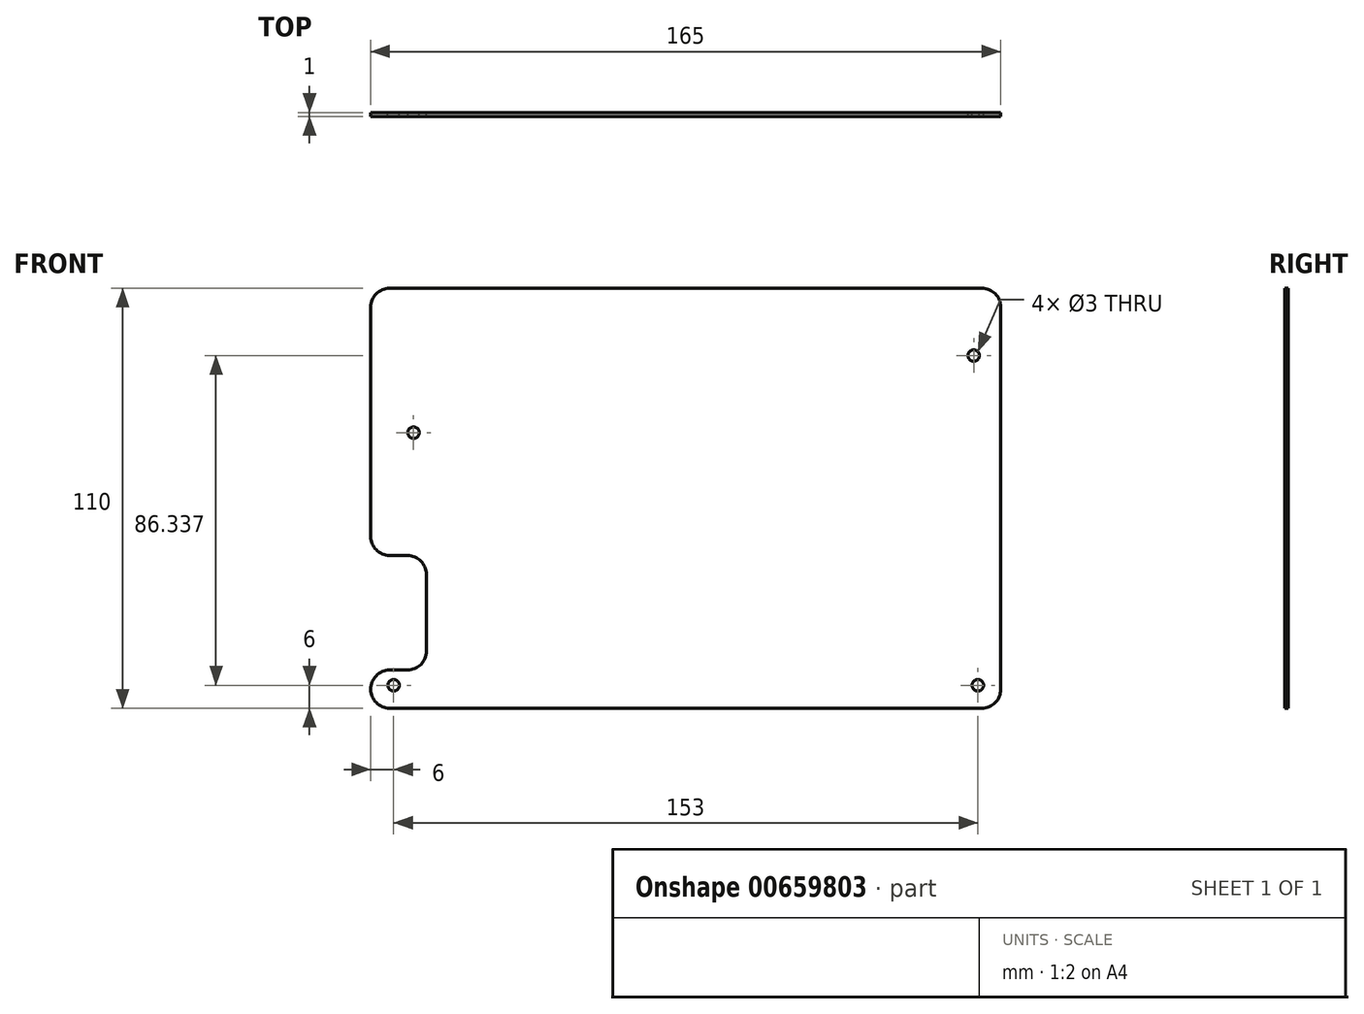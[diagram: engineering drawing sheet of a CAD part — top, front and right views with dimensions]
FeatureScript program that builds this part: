
annotation { "Feature Type Name" : "Feature", "Feature Type Description" : "" }
export const myFeature = defineFeature(function(context is Context, id is Id, definition is map)
    precondition{}
    {
        {
            var Q0;
            Q0=qCreatedBy(makeId("Front.planeOp"),FACE);
            var sketch = newSketch(context, id + "F0", { "sketchPlane" : qUnion([Q0])});
            skLineSegment(sketch, "E0.bottom", {"start": v(5, 0) * mm, "end": v(160, 0) * mm});
            skLineSegment(sketch, "E0.top", {"start": v(0, -110) * mm, "end": v(160, -110) * mm});
            skLineSegment(sketch, "E0.left", {"start": v(0, -105) * mm, "end": v(0, -110) * mm});
            skLineSegment(sketch, "E0.right", {"start": v(165, -5) * mm, "end": v(165, -105) * mm});
            skLineSegment(sketch, "E1.bottom", {"start": v(5, -100) * mm, "end": v(9.61, -100) * mm});
            skLineSegment(sketch, "E1.top", {"start": v(5, -70) * mm, "end": v(9.61, -70) * mm});
            skLineSegment(sketch, "E1.right", {"start": v(14.61, -95) * mm, "end": v(14.61, -75) * mm});
            skCircle(sketch, "E2", {"center": v(159, -104) * mm, "radius": 1.5 * mm});
            skCircle(sketch, "E3", {"center": v(157.92, -17.66) * mm, "radius": 1.5 * mm});
            skCircle(sketch, "E4", {"center": v(6, -104) * mm, "radius": 1.5 * mm});
            skLineSegment(sketch, "E5.bottom", {"start": v(5, -110) * mm, "end": v(6, -110) * mm});
            skLineSegment(sketch, "E5.left", {"start": v(0, -105) * mm, "end": v(0, -104) * mm});
            skLineSegment(sketch, "E6.left", {"start": v(0, -65) * mm, "end": v(0, -45) * mm});
            skCircle(sketch, "E7", {"center": v(11.22, -37.85) * mm, "radius": 1.5 * mm});
            skPoint(sketch, "E8.visualSharp", {"position": v(14.61, -70) * mm});
            skArc(sketch, "E8.filletArc", {"start": v(14.61, -75) * mm, "mid": v(13.15, -71.46) * mm, "end": v(9.61, -70) * mm});
            skPoint(sketch, "E9.visualSharp", {"position": v(14.61, -100) * mm});
            skArc(sketch, "E9.filletArc", {"start": v(9.61, -100) * mm, "mid": v(13.15, -98.54) * mm, "end": v(14.61, -95) * mm});
            skPoint(sketch, "E10.visualSharp", {"position": v(0, -110) * mm});
            skArc(sketch, "E10.filletArc", {"start": v(0, -105) * mm, "mid": v(1.46, -108.54) * mm, "end": v(5, -110) * mm});
            skPoint(sketch, "E11.visualSharp", {"position": v(0, 0) * mm});
            skArc(sketch, "E11.filletArc", {"start": v(5, 0) * mm, "mid": v(1.46, -1.46) * mm, "end": v(0, -5) * mm});
            skPoint(sketch, "E12.visualSharp", {"position": v(165, -110) * mm});
            skArc(sketch, "E12.filletArc", {"start": v(160, -110) * mm, "mid": v(163.54, -108.54) * mm, "end": v(165, -105) * mm});
            skPoint(sketch, "E13.visualSharp", {"position": v(165, 0) * mm});
            skArc(sketch, "E13.filletArc", {"start": v(165, -5) * mm, "mid": v(163.54, -1.46) * mm, "end": v(160, 0) * mm});
            skPoint(sketch, "E14.visualSharp", {"position": v(0, -70) * mm});
            skArc(sketch, "E14.filletArc", {"start": v(0, -65) * mm, "mid": v(1.46, -68.54) * mm, "end": v(5, -70) * mm});
            skArc(sketch, "E15.filletArc", {"start": v(5, -100) * mm, "mid": v(1.46, -101.46) * mm, "end": v(0, -105) * mm});
            skLineSegment(sketch, "E16", {"start": v(0, -45) * mm, "end": v(0, -5) * mm});
            skSolve(sketch);
        }
        {
            var Q0;
            Q0=makeQuery(id+"F0.imprint","IMPRINT",FACE,{"disambiguationData":[TD([[makeQuery(id+"F0.imprint","IMPRINT",EDGE,{"derivedFrom":sQuery(id+"F0.wireOp",EDGE,"E0.bottom")}),-1.0]])]});
            extrude(context, id + "F1", {"entities" : qUnion([Q0]), "depth" : 1 * mm, "offsetDistance" : 25 * mm});
        }
    });
